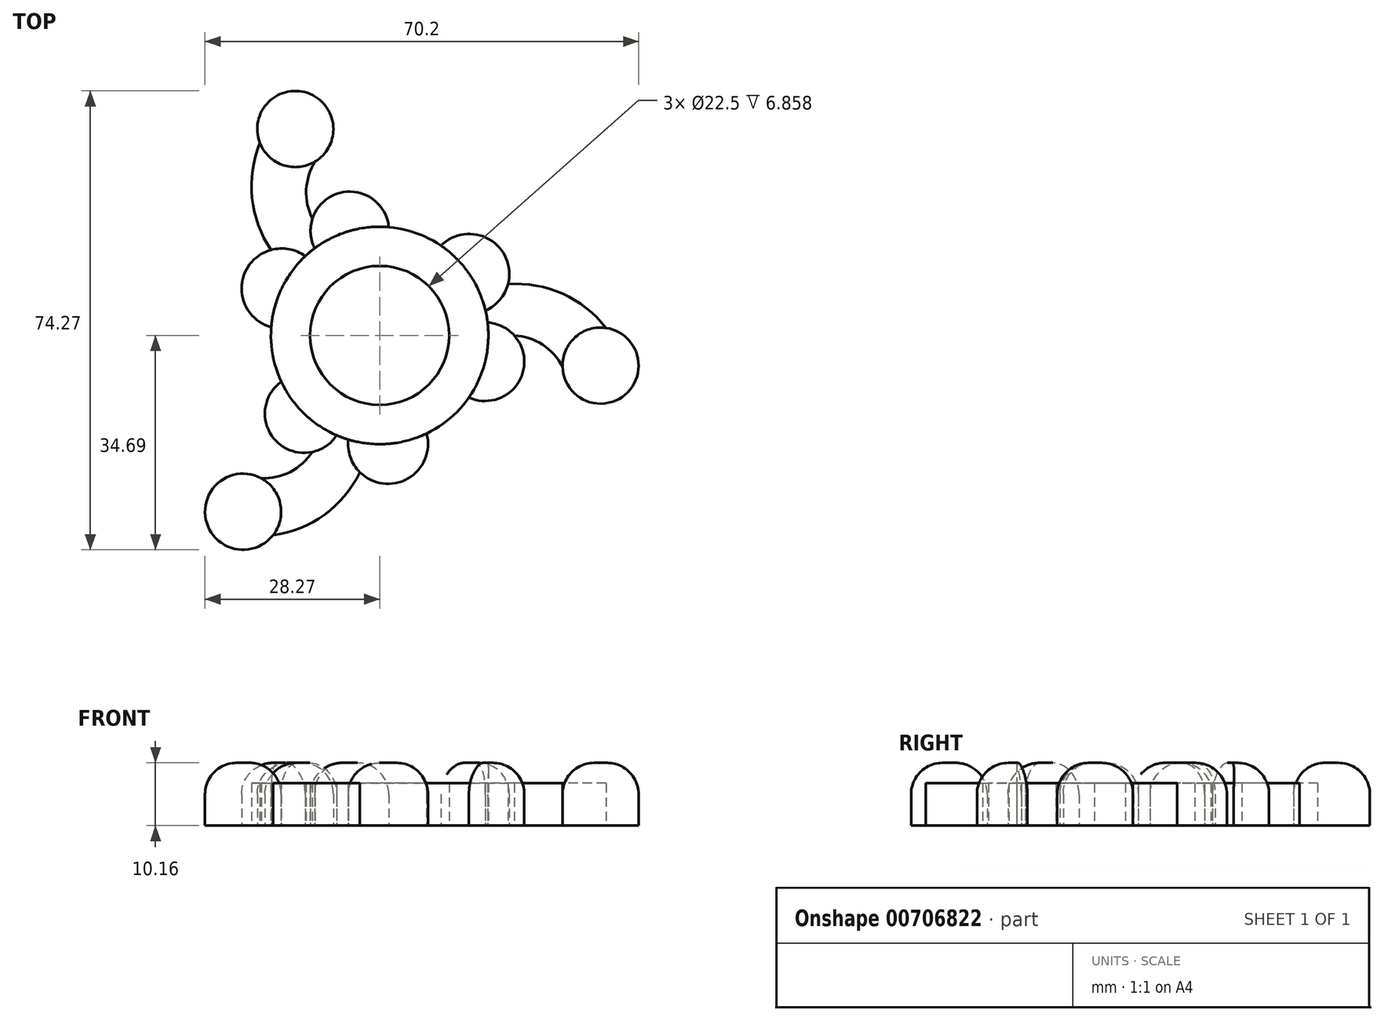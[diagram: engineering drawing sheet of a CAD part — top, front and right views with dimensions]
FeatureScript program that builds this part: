
annotation { "Feature Type Name" : "Feature", "Feature Type Description" : "" }
export const myFeature = defineFeature(function(context is Context, id is Id, definition is map)
    precondition{}
    {
        {
            var Q0;
            Q0=qCreatedBy(makeId("Top.planeOp"),FACE);
            var sketch = newSketch(context, id + "F0", { "sketchPlane" : qUnion([Q0])});
            skCircle(sketch, "E0", {"center": v(0, 0) * mm, "radius": 11.25 * mm});
            skCircle(sketch, "E1", {"center": v(0, 0) * mm, "radius": 17.6 * mm});
            skArc(sketch, "E2", {"start": v(-12.05, 12.83) * mm, "mid": v(-21.72, 10.4) * mm, "end": v(-17.55, 1.34) * mm});
            skArc(sketch, "E3", {"start": v(1.47, 17.54) * mm, "mid": v(-6.6, 23.02) * mm, "end": v(-10.53, 14.1) * mm});
            skArc(sketch, "E4", {"start": v(-19.38, 31.14) * mm, "mid": v(-20.65, 22.27) * mm, "end": v(-17.58, 13.85) * mm});
            skArc(sketch, "E5", {"start": v(-10.44, 28.16) * mm, "mid": v(-11.88, 23.58) * mm, "end": v(-10.88, 18.89) * mm});
            skCircle(sketch, "E6", {"center": v(-13.65, 33.41) * mm, "radius": 6.16 * mm});
            skPoint(sketch, "E6.third.point", {"position": v(-10.44, 38.67) * mm});
            skArc(sketch, "E7.trimOffspring", {"start": v(-10.55, 3.92) * mm, "mid": v(-10.03, 4.8) * mm, "end": v(-9.67, 5.76) * mm});
            skCircle(sketch, "E8.1.0", {"center": v(35.76, -4.88) * mm, "radius": 6.16 * mm});
            skArc(sketch, "E8.1.1", {"start": v(36.66, 1.21) * mm, "mid": v(29.61, 6.75) * mm, "end": v(20.78, 8.3) * mm});
            skArc(sketch, "E8.1.2", {"start": v(29.6, -5.04) * mm, "mid": v(26.37, -1.5) * mm, "end": v(21.8, -0.02) * mm});
            skArc(sketch, "E8.1.3", {"start": v(14.45, -10.05) * mm, "mid": v(23.24, -5.8) * mm, "end": v(17.48, 2.07) * mm});
            skArc(sketch, "E8.1.4", {"start": v(17.13, 4.03) * mm, "mid": v(19.86, 13.61) * mm, "end": v(9.93, 14.53) * mm});
            skCircle(sketch, "E8.2.0", {"center": v(-22.11, -28.53) * mm, "radius": 6.16 * mm});
            skArc(sketch, "E8.2.1", {"start": v(-17.28, -32.36) * mm, "mid": v(-8.96, -29.02) * mm, "end": v(-3.2, -22.15) * mm});
            skArc(sketch, "E8.2.2", {"start": v(-19.17, -23.12) * mm, "mid": v(-14.48, -22.08) * mm, "end": v(-10.91, -18.87) * mm});
            skArc(sketch, "E8.2.3", {"start": v(-15.93, -7.5) * mm, "mid": v(-16.64, -17.22) * mm, "end": v(-6.94, -16.17) * mm});
            skArc(sketch, "E8.2.4", {"start": v(-5.08, -16.85) * mm, "mid": v(1.86, -24) * mm, "end": v(7.61, -15.87) * mm});
            skLineSegment(sketch, "E8.anchor1", {"start": v(0, 0) * mm, "end": v(-13.65, 33.41) * mm, "construction": true});
            skLineSegment(sketch, "E8.anchor2", {"start": v(0, 0) * mm, "end": v(-22.11, -28.53) * mm, "construction": true});
            skSolve(sketch);
        }
        {
            var Q0;
            {var subQ0=sQuery(id+"F0.wireOp",EDGE,"E6");var subQ1=makeQuery(id+"F0.imprint","INTERSECT",VERTEX,{"derivedFrom":[sQuery(id+"F0.wireOp",EDGE,"E4"),subQ0]});Q0=makeQuery(id+"F0.imprint","IMPRINT",FACE,{"disambiguationData":[TD([[makeQuery(id+"F0.imprint","IMPRINT",EDGE,{"disambiguationData":[TD([[subQ1,-1.0]])],"derivedFrom":subQ0}),1.0]])]});}
            var Q1;
            {var subQ0=sQuery(id+"F0.wireOp",EDGE,"E8.1.0");var subQ1=makeQuery(id+"F0.imprint","INTERSECT",VERTEX,{"derivedFrom":[subQ0,sQuery(id+"F0.wireOp",EDGE,"E8.1.1")]});Q1=makeQuery(id+"F0.imprint","IMPRINT",FACE,{"disambiguationData":[TD([[makeQuery(id+"F0.imprint","IMPRINT",EDGE,{"disambiguationData":[TD([[subQ1,-1.0]])],"derivedFrom":subQ0}),1.0]])]});}
            var Q2;
            {var subQ0=sQuery(id+"F0.wireOp",EDGE,"E8.2.0");var subQ1=makeQuery(id+"F0.imprint","INTERSECT",VERTEX,{"derivedFrom":[subQ0,sQuery(id+"F0.wireOp",EDGE,"E8.2.1")]});Q2=makeQuery(id+"F0.imprint","IMPRINT",FACE,{"disambiguationData":[TD([[makeQuery(id+"F0.imprint","IMPRINT",EDGE,{"disambiguationData":[TD([[subQ1,-1.0]])],"derivedFrom":subQ0}),1.0]])]});}
            extrude(context, id + "F1", {"entities" : qUnion([Q0, Q1, Q2]), "depth" : 10.16 * mm, "offsetDistance" : 25.4 * mm});
        }
        {
            var Q0;
            {var subQ0=sQuery(id+"F0.wireOp",EDGE,"E4");Q0=makeQuery(id+"F0.imprint","IMPRINT",FACE,{"disambiguationData":[TD([[makeQuery(id+"F0.imprint","IMPRINT",EDGE,{"derivedFrom":subQ0}),1.0]])]});}
            var Q1;
            {var subQ1=sQuery(id+"F0.wireOp",EDGE,"E8.1.1");Q1=makeQuery(id+"F0.imprint","IMPRINT",FACE,{"disambiguationData":[TD([[makeQuery(id+"F0.imprint","IMPRINT",EDGE,{"derivedFrom":subQ1}),1.0]])]});}
            var Q2;
            {var subQ1=sQuery(id+"F0.wireOp",EDGE,"E8.2.1");Q2=makeQuery(id+"F0.imprint","IMPRINT",FACE,{"disambiguationData":[TD([[makeQuery(id+"F0.imprint","IMPRINT",EDGE,{"derivedFrom":subQ1}),1.0]])]});}
            extrude(context, id + "F2", {"entities" : qUnion([Q0, Q1, Q2]), "depth" : 6.86 * mm, "offsetDistance" : 25.4 * mm});
        }
        {
            var Q0;
            {var subQ0=sQuery(id+"F0.wireOp",EDGE,"E2");var subQ1=sQuery(id+"F0.wireOp",EDGE,"E1");var subQ2=makeQuery(id+"F0.imprint","INTERSECT",VERTEX,{"disambiguationData":[OD(0.0)],"derivedFrom":[subQ1,subQ0]});Q0=makeQuery(id+"F0.imprint","IMPRINT",FACE,{"disambiguationData":[TD([[makeQuery(id+"F0.imprint","IMPRINT",EDGE,{"disambiguationData":[TD([[subQ2,-1.0]])],"derivedFrom":subQ1}),-1.0]])]});}
            var Q1;
            {var subQ0=sQuery(id+"F0.wireOp",EDGE,"E3");var subQ1=sQuery(id+"F0.wireOp",EDGE,"E1");var subQ2=makeQuery(id+"F0.imprint","INTERSECT",VERTEX,{"disambiguationData":[OD(0.0)],"derivedFrom":[subQ1,subQ0]});Q1=makeQuery(id+"F0.imprint","IMPRINT",FACE,{"disambiguationData":[TD([[makeQuery(id+"F0.imprint","IMPRINT",EDGE,{"disambiguationData":[TD([[subQ2,-1.0]])],"derivedFrom":subQ1}),-1.0]])]});}
            var Q2;
            {var subQ0=sQuery(id+"F0.wireOp",EDGE,"E8.1.4");var subQ1=sQuery(id+"F0.wireOp",EDGE,"E1");var subQ2=makeQuery(id+"F0.imprint","INTERSECT",VERTEX,{"disambiguationData":[OD(0.0)],"derivedFrom":[subQ1,subQ0]});Q2=makeQuery(id+"F0.imprint","IMPRINT",FACE,{"disambiguationData":[TD([[makeQuery(id+"F0.imprint","IMPRINT",EDGE,{"disambiguationData":[TD([[subQ2,-1.0]])],"derivedFrom":subQ1}),-1.0]])]});}
            var Q3;
            {var subQ0=sQuery(id+"F0.wireOp",EDGE,"E8.1.3");var subQ1=sQuery(id+"F0.wireOp",EDGE,"E1");var subQ2=makeQuery(id+"F0.imprint","INTERSECT",VERTEX,{"disambiguationData":[OD(0.0)],"derivedFrom":[subQ1,subQ0]});Q3=makeQuery(id+"F0.imprint","IMPRINT",FACE,{"disambiguationData":[TD([[makeQuery(id+"F0.imprint","IMPRINT",EDGE,{"disambiguationData":[TD([[subQ2,-1.0]])],"derivedFrom":subQ1}),-1.0]])]});}
            var Q4;
            {var subQ0=sQuery(id+"F0.wireOp",EDGE,"E8.2.4");var subQ1=sQuery(id+"F0.wireOp",EDGE,"E1");var subQ2=makeQuery(id+"F0.imprint","INTERSECT",VERTEX,{"disambiguationData":[OD(0.0)],"derivedFrom":[subQ1,subQ0]});Q4=makeQuery(id+"F0.imprint","IMPRINT",FACE,{"disambiguationData":[TD([[makeQuery(id+"F0.imprint","IMPRINT",EDGE,{"disambiguationData":[TD([[subQ2,-1.0]])],"derivedFrom":subQ1}),-1.0]])]});}
            var Q5;
            {var subQ0=sQuery(id+"F0.wireOp",EDGE,"E8.2.3");var subQ1=sQuery(id+"F0.wireOp",EDGE,"E1");var subQ2=makeQuery(id+"F0.imprint","INTERSECT",VERTEX,{"disambiguationData":[OD(0.0)],"derivedFrom":[subQ1,subQ0]});Q5=makeQuery(id+"F0.imprint","IMPRINT",FACE,{"disambiguationData":[TD([[makeQuery(id+"F0.imprint","IMPRINT",EDGE,{"disambiguationData":[TD([[subQ2,-1.0]])],"derivedFrom":subQ1}),-1.0]])]});}
            extrude(context, id + "F3", {"entities" : qUnion([Q0, Q1, Q2, Q3, Q4, Q5]), "depth" : 10.16 * mm, "offsetDistance" : 25.4 * mm});
        }
        {
            var Q0;
            {var subQ12=sQuery(id+"F0.wireOp",EDGE,"E7.trimOffspring");var subQ13=sQuery(id+"F0.wireOp",EDGE,"E0");var subQ14=makeQuery(id+"F0.imprint","INTERSECT",VERTEX,{"disambiguationData":[OD(0.0)],"derivedFrom":[subQ13,subQ12]});Q0=makeQuery(id+"F0.imprint","IMPRINT",FACE,{"disambiguationData":[TD([[makeQuery(id+"F0.imprint","IMPRINT",EDGE,{"disambiguationData":[TD([[subQ14,1.0]])],"derivedFrom":subQ13}),-1.0]])]});}
            extrude(context, id + "F4", {"entities" : qUnion([Q0]), "depth" : 6.86 * mm, "offsetDistance" : 25.4 * mm});
        }
        {
            var Q0;
            Q0=makeQuery(id+"F1.opExtrude","CAP_EDGE",EDGE,{"disambiguationData":[OSD([sQuery(id+"F0.wireOp",EDGE,"E6")])],"isStart":false});
            fillet(context, id + "F5", {"entities" : qUnion([Q0]), "radius" : 5.08 * mm, "tangentPropagation" : true, "allowEdgeOverflow" : false});
        }
        {
            var Q0;
            Q0=makeQuery(id+"F3.opExtrude","CAP_EDGE",EDGE,{"disambiguationData":[OSD([sQuery(id+"F0.wireOp",EDGE,"E3")])],"isStart":false});
            var Q1;
            Q1=makeQuery(id+"F3.opExtrude","CAP_EDGE",EDGE,{"disambiguationData":[OSD([sQuery(id+"F0.wireOp",EDGE,"E2")])],"isStart":false});
            var Q2;
            Q2=makeQuery(id+"F3.opExtrude","CAP_EDGE",EDGE,{"disambiguationData":[OSD([sQuery(id+"F0.wireOp",EDGE,"E8.1.4")])],"isStart":false});
            var Q3;
            Q3=makeQuery(id+"F3.opExtrude","CAP_EDGE",EDGE,{"disambiguationData":[OSD([sQuery(id+"F0.wireOp",EDGE,"E8.1.3")])],"isStart":false});
            var Q4;
            Q4=makeQuery(id+"F1.opExtrude","CAP_EDGE",EDGE,{"disambiguationData":[OSD([sQuery(id+"F0.wireOp",EDGE,"E8.1.0")])],"isStart":false});
            var Q5;
            Q5=makeQuery(id+"F3.opExtrude","CAP_EDGE",EDGE,{"disambiguationData":[OSD([sQuery(id+"F0.wireOp",EDGE,"E8.2.3")])],"isStart":false});
            var Q6;
            Q6=makeQuery(id+"F3.opExtrude","CAP_EDGE",EDGE,{"disambiguationData":[OSD([sQuery(id+"F0.wireOp",EDGE,"E8.2.4")])],"isStart":false});
            var Q7;
            Q7=makeQuery(id+"F1.opExtrude","CAP_EDGE",EDGE,{"disambiguationData":[OSD([sQuery(id+"F0.wireOp",EDGE,"E8.2.0")])],"isStart":false});
            fillet(context, id + "F6", {"entities" : qUnion([Q0, Q1, Q2, Q3, Q4, Q5, Q6, Q7]), "radius" : 5.08 * mm, "tangentPropagation" : true, "allowEdgeOverflow" : false});
        }
    });
